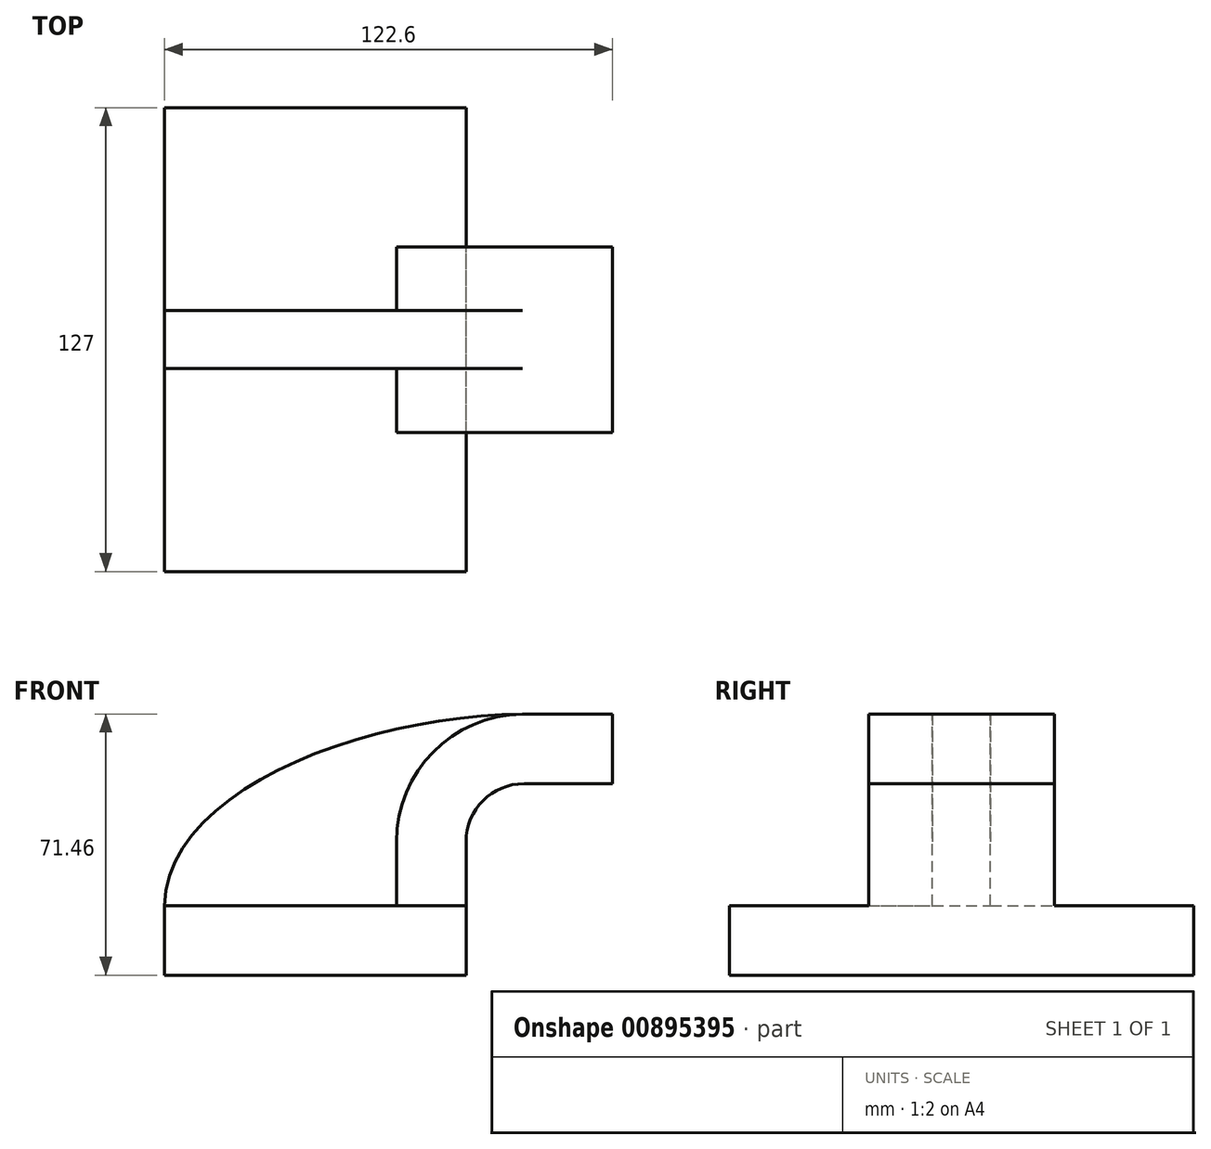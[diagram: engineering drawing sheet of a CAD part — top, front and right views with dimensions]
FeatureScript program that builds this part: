
annotation { "Feature Type Name" : "Feature", "Feature Type Description" : "" }
export const myFeature = defineFeature(function(context is Context, id is Id, definition is map)
    precondition{}
    {
        {
            var Q0;
            Q0=qCreatedBy(makeId("Front.planeOp"),FACE);
            var sketch = newSketch(context, id + "F0", { "sketchPlane" : qUnion([Q0])});
            skLineSegment(sketch, "E0.bottom", {"start": v(-41.28, 9.52) * mm, "end": v(41.28, 9.53) * mm});
            skLineSegment(sketch, "E0.top", {"start": v(-41.28, -9.53) * mm, "end": v(41.28, -9.53) * mm});
            skLineSegment(sketch, "E0.left", {"start": v(-41.28, 9.52) * mm, "end": v(-41.27, -9.53) * mm});
            skLineSegment(sketch, "E0.right", {"start": v(41.28, 9.53) * mm, "end": v(41.28, -9.52) * mm});
            skPoint(sketch, "E0.middle", {"position": v(0, 0) * mm});
            skLineSegment(sketch, "E1.bottom", {"start": v(60.32, 66.68) * mm, "end": v(111.12, 66.68) * mm});
            skLineSegment(sketch, "E1.top", {"start": v(60.32, 38.1) * mm, "end": v(111.12, 38.1) * mm});
            skLineSegment(sketch, "E1.left", {"start": v(60.32, 66.68) * mm, "end": v(60.32, 38.1) * mm});
            skLineSegment(sketch, "E1.right", {"start": v(111.12, 66.68) * mm, "end": v(111.12, 38.1) * mm});
            skPoint(sketch, "E1.middle", {"position": v(85.72, 52.39) * mm});
            skLineSegment(sketch, "E2", {"start": v(41.27, 9.53) * mm, "end": v(41.27, 27) * mm});
            skArc(sketch, "E3", {"start": v(41.27, 27) * mm, "mid": v(45.92, 38.23) * mm, "end": v(57.15, 42.88) * mm});
            skLineSegment(sketch, "E4", {"start": v(57.15, 42.88) * mm, "end": v(81.32, 42.88) * mm});
            skLineSegment(sketch, "E5.0", {"start": v(57.15, 61.93) * mm, "end": v(81.32, 61.93) * mm});
            skArc(sketch, "E5.1", {"start": v(22.22, 27) * mm, "mid": v(32.45, 51.7) * mm, "end": v(57.15, 61.93) * mm});
            skLineSegment(sketch, "E5.2", {"start": v(22.22, 9.53) * mm, "end": v(22.22, 27) * mm});
            skFitSpline(sketch, "E6", {"points": [v(-41.28, 9.52) * mm, v(57.15, 61.93) * mm], "startDerivative": vector(3.1, 97.64) * mm, "endDerivative": vector(126.85, 0.63) * mm});
            skLineSegment(sketch, "E7", {"start": v(81.32, 61.93) * mm, "end": v(81.32, 42.88) * mm});
            skSolve(sketch);
        }
        {
            var Q0;
            Q0=makeQuery(id+"F0.imprint","IMPRINT",FACE,{"disambiguationData":[TD([[makeQuery(id+"F0.imprint","IMPRINT",EDGE,{"derivedFrom":sQuery(id+"F0.wireOp",EDGE,"E0.top")}),1.0]])]});
            extrude(context, id + "F1", {"entities" : qUnion([Q0]), "endBound" : BoundingType.SYMMETRIC, "depth" : 127 * mm, "offsetDistance" : 25.4 * mm});
        }
        {
            var Q0;
            {var subQ3=sQuery(id+"F0.wireOp",EDGE,"E5.2");Q0=makeQuery(id+"F0.imprint","IMPRINT",FACE,{"disambiguationData":[TD([[makeQuery(id+"F0.imprint","IMPRINT",EDGE,{"derivedFrom":subQ3}),1.0]])]});}
            extrude(context, id + "F2", {"entities" : qUnion([Q0]), "operationType" : NewBodyOperationType.ADD, "endBound" : BoundingType.SYMMETRIC, "depth" : 15.88 * mm, "offsetDistance" : 25.4 * mm});
        }
        {
            var Q0;
            {var subQ5=sQuery(id+"F0.wireOp",EDGE,"E7");Q0=makeQuery(id+"F0.imprint","IMPRINT",FACE,{"disambiguationData":[TD([[makeQuery(id+"F0.imprint","IMPRINT",EDGE,{"derivedFrom":subQ5}),-1.0]])]});}
            var Q1;
            {var subQ1=sQuery(id+"F0.wireOp",EDGE,"E2");Q1=makeQuery(id+"F0.imprint","IMPRINT",FACE,{"disambiguationData":[TD([[makeQuery(id+"F0.imprint","IMPRINT",EDGE,{"derivedFrom":subQ1}),1.0]])]});}
            extrude(context, id + "F3", {"entities" : qUnion([Q0, Q1]), "operationType" : NewBodyOperationType.ADD, "endBound" : BoundingType.SYMMETRIC, "depth" : 50.8 * mm, "offsetDistance" : 25.4 * mm});
        }
    });
